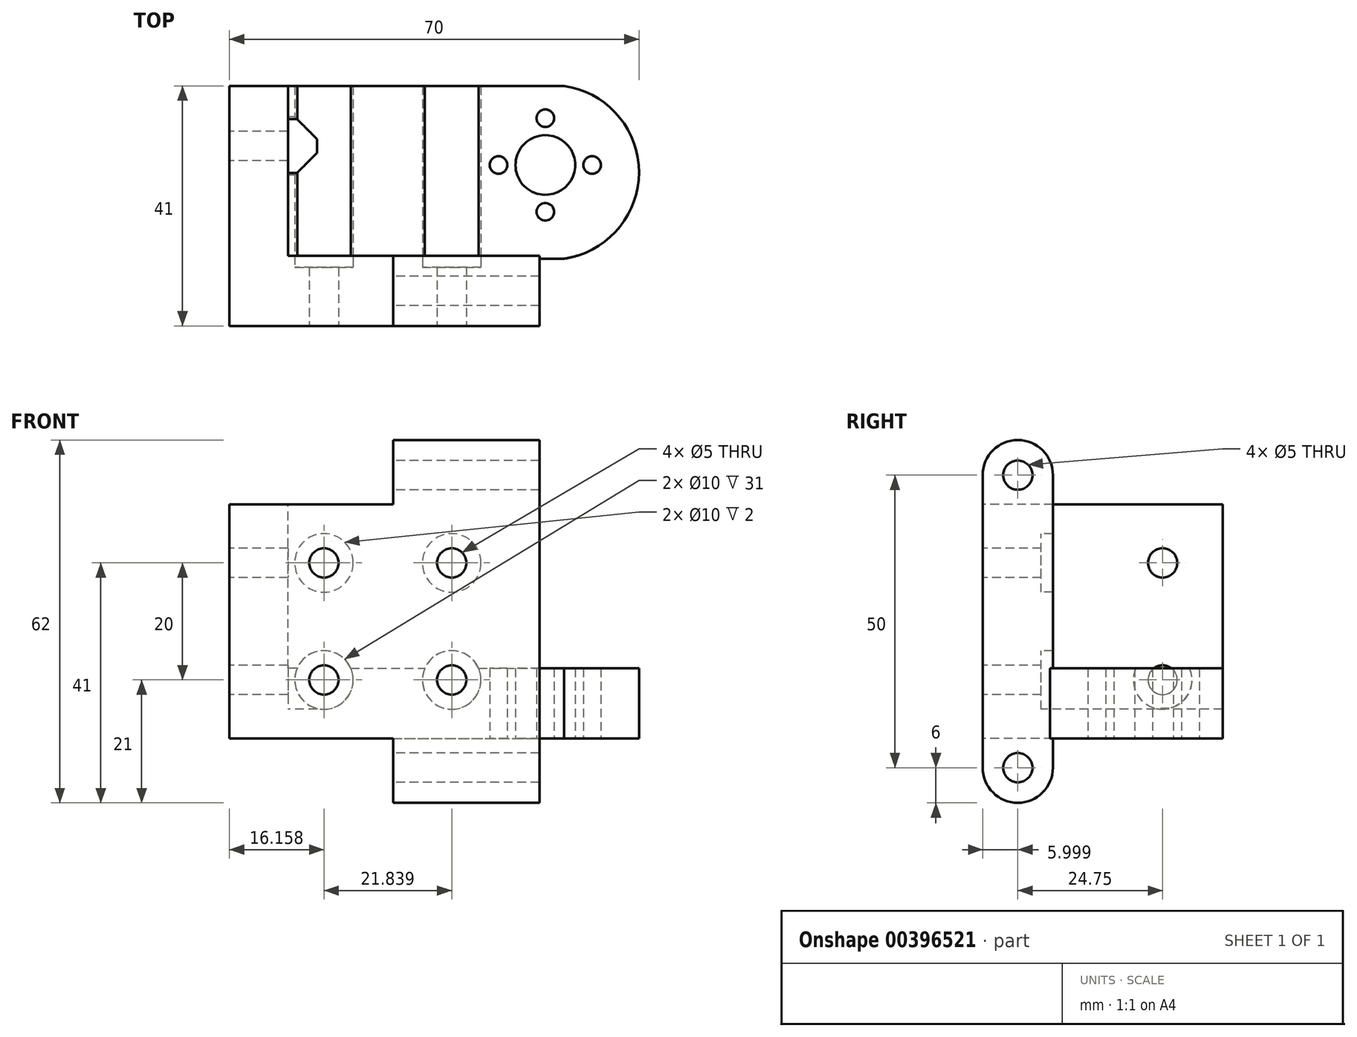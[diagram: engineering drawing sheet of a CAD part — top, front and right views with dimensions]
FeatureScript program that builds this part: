
annotation { "Feature Type Name" : "Feature", "Feature Type Description" : "" }
export const myFeature = defineFeature(function(context is Context, id is Id, definition is map)
    precondition{}
    {
        {
            var Q0;
            Q0=qCreatedBy(makeId("Top.planeOp"),FACE);
            var sketch = newSketch(context, id + "F0", { "sketchPlane" : qUnion([Q0])});
            skLineSegment(sketch, "E0.bottom", {"start": v(-287.66, 67.89) * mm, "end": v(-234.66, 67.89) * mm});
            skLineSegment(sketch, "E0.top", {"start": v(-287.66, 26.89) * mm, "end": v(-274.66, 26.89) * mm});
            skLineSegment(sketch, "E0.left", {"start": v(-287.66, 67.89) * mm, "end": v(-287.66, 26.89) * mm});
            skLineSegment(sketch, "E1.top", {"start": v(-234.66, 6.89) * mm, "end": v(-274.66, 6.89) * mm});
            skLineSegment(sketch, "E1.left", {"start": v(-234.66, 26.89) * mm, "end": v(-234.66, 6.89) * mm});
            skLineSegment(sketch, "E1.right", {"start": v(-274.66, 26.89) * mm, "end": v(-274.66, 6.89) * mm});
            skLineSegment(sketch, "E2.bottom", {"start": v(-234.66, 67.89) * mm, "end": v(-230.46, 67.89) * mm});
            skLineSegment(sketch, "E2.top", {"start": v(-234.66, 38.39) * mm, "end": v(-230.46, 38.39) * mm});
            skArc(sketch, "E3", {"start": v(-230.46, 38.39) * mm, "mid": v(-217.66, 53.14) * mm, "end": v(-230.46, 67.89) * mm});
            skLineSegment(sketch, "E4", {"start": v(-233.66, 54.39) * mm, "end": v(-287.66, 54.39) * mm, "construction": true});
            skCircle(sketch, "E5", {"center": v(-233.66, 54.39) * mm, "radius": 5.1 * mm});
            skLineSegment(sketch, "E6.trimOffspring", {"start": v(-234.66, 38.39) * mm, "end": v(-234.66, 26.89) * mm});
            skLineSegment(sketch, "E7", {"start": v(-233.66, 54.39) * mm, "end": v(-233.66, 62.39) * mm, "construction": true});
            skLineSegment(sketch, "E8", {"start": v(-233.66, 54.39) * mm, "end": v(-233.66, 46.39) * mm, "construction": true});
            skLineSegment(sketch, "E9", {"start": v(-233.66, 54.39) * mm, "end": v(-225.66, 54.39) * mm, "construction": true});
            skLineSegment(sketch, "E10", {"start": v(-233.66, 54.39) * mm, "end": v(-241.66, 54.39) * mm, "construction": true});
            skCircle(sketch, "E11", {"center": v(-241.66, 54.39) * mm, "radius": 1.5 * mm});
            skCircle(sketch, "E12", {"center": v(-233.66, 62.39) * mm, "radius": 1.5 * mm});
            skCircle(sketch, "E13", {"center": v(-225.66, 54.39) * mm, "radius": 1.5 * mm});
            skCircle(sketch, "E14", {"center": v(-233.66, 46.39) * mm, "radius": 1.5 * mm});
            skLineSegment(sketch, "E15", {"start": v(-233.66, 54.39) * mm, "end": v(-233.66, 26.89) * mm, "construction": true});
            skSolve(sketch);
        }
        {
            var Q0;
            Q0 = qSketchRegion(id + "F0", true);
            extrude(context, id + "F1", {"entities" : qUnion([Q0]), "depth" : 40 * mm});
        }
        {
            var Q0;
            Q0=makeQuery(id+"F1.opExtrude","CAP_FACE",FACE,{"disambiguationData":[OSD([sQuery(id+"F0.wireOp",EDGE,"E0.bottom"),sQuery(id+"F0.wireOp",EDGE,"E0.top"),sQuery(id+"F0.wireOp",EDGE,"E0.left"),sQuery(id+"F0.wireOp",EDGE,"E1.top"),sQuery(id+"F0.wireOp",EDGE,"E1.left"),sQuery(id+"F0.wireOp",EDGE,"E1.right"),sQuery(id+"F0.wireOp",EDGE,"E2.bottom"),sQuery(id+"F0.wireOp",EDGE,"E2.top"),sQuery(id+"F0.wireOp",EDGE,"E3"),sQuery(id+"F0.wireOp",EDGE,"E5"),sQuery(id+"F0.wireOp",EDGE,"E6.trimOffspring"),sQuery(id+"F0.wireOp",EDGE,"E11"),sQuery(id+"F0.wireOp",EDGE,"E12"),sQuery(id+"F0.wireOp",EDGE,"E13"),sQuery(id+"F0.wireOp",EDGE,"E14")])],"isStart":false});
            var sketch = newSketch(context, id + "F2", { "sketchPlane" : qUnion([Q0])});
            skCircle(sketch, "E16", {"center": v(-233.66, 54.39) * mm, "radius": 11.5 * mm});
            skSolve(sketch);
        }
        {
            var Q0;
            Q0 = qSketchRegion(id + "F2", true);
            extrude(context, id + "F3", {"entities" : qUnion([Q0]), "operationType" : NewBodyOperationType.REMOVE, "oppositeDirection" : true, "depth" : (40 - 12) * mm});
        }
        {
            var Q0;
            Q0=makeQuery(id+"F1.opExtrude","SWEPT_FACE",FACE,{"disambiguationData":[OSD([sQuery(id+"F0.wireOp",EDGE,"E0.left")])]});
            var sketch = newSketch(context, id + "F4", { "sketchPlane" : qUnion([Q0])});
            skLineSegment(sketch, "E17.bottom", {"start": v(-26.89, 20) * mm, "end": v(-38.89, 20) * mm, "construction": true});
            skLineSegment(sketch, "E17.top", {"start": v(-26.89, 45) * mm, "end": v(-38.89, 45) * mm, "construction": true});
            skLineSegment(sketch, "E17.left", {"start": v(-26.89, 20) * mm, "end": v(-26.89, 45) * mm});
            skLineSegment(sketch, "E17.right", {"start": v(-38.89, 20) * mm, "end": v(-38.89, 45) * mm});
            skLineSegment(sketch, "E18.MirrorCS", {"start": v(-38.89, 20) * mm, "end": v(-38.89, -5) * mm});
            skLineSegment(sketch, "E19.MirrorCS", {"start": v(-26.89, 20) * mm, "end": v(-26.89, -5) * mm});
            skLineSegment(sketch, "E20.MirrorCS", {"start": v(-26.89, -5) * mm, "end": v(-38.89, -5) * mm, "construction": true});
            skCircle(sketch, "E21", {"center": v(-32.89, 45) * mm, "radius": 6 * mm});
            skCircle(sketch, "E22", {"center": v(-32.89, -5) * mm, "radius": 6 * mm});
            skLineSegment(sketch, "E23", {"start": v(-32.89, 20) * mm, "end": v(-32.89, 51) * mm, "construction": true});
            skCircle(sketch, "E24", {"center": v(-32.89, 45) * mm, "radius": 2.5 * mm});
            skCircle(sketch, "E25", {"center": v(-32.89, -5) * mm, "radius": 2.5 * mm});
            skSolve(sketch);
        }
        {
            var Q0;
            Q0 = qSketchRegion(id + "F4", true);
            extrude(context, id + "F5", {"entities" : qUnion([Q0]), "operationType" : NewBodyOperationType.ADD, "oppositeDirection" : true, "depth" : 53 * mm, "hasSecondDirection" : true, "secondDirectionOppositeDirection" : true, "secondDirectionDepth" : (53 - 25) * mm});
        }
        {
            var Q0;
            Q0=makeQuery(id+"F1.opExtrude","SWEPT_FACE",FACE,{"disambiguationData":[OSD([sQuery(id+"F0.wireOp",EDGE,"E0.bottom"),sQuery(id+"F0.wireOp",EDGE,"E2.bottom")])]});
            var sketch = newSketch(context, id + "F6", { "sketchPlane" : qUnion([Q0])});
            skLineSegment(sketch, "E26.bottom", {"start": v(287.66, 40) * mm, "end": v(277.66, 40) * mm, "construction": true});
            skLineSegment(sketch, "E26.top", {"start": v(287.66, 0) * mm, "end": v(277.66, 0) * mm, "construction": true});
            skLineSegment(sketch, "E26.left", {"start": v(287.66, 40) * mm, "end": v(287.66, 0) * mm, "construction": true});
            skLineSegment(sketch, "E26.right", {"start": v(277.66, 40) * mm, "end": v(277.66, 0) * mm, "construction": true});
            skLineSegment(sketch, "E27.top", {"start": v(287.66, 12) * mm, "end": v(277.66, 12) * mm, "construction": true});
            skLineSegment(sketch, "E27.left", {"start": v(287.66, 0) * mm, "end": v(287.66, 12) * mm, "construction": true});
            skLineSegment(sketch, "E27.right", {"start": v(277.66, 0) * mm, "end": v(277.66, 12) * mm, "construction": true});
            skLineSegment(sketch, "E28.bottom", {"start": v(277.66, 12) * mm, "end": v(200.17, 12) * mm});
            skLineSegment(sketch, "E28.top", {"start": v(277.66, 42.16) * mm, "end": v(200.17, 42.16) * mm});
            skLineSegment(sketch, "E28.left", {"start": v(277.66, 12) * mm, "end": v(277.66, 42.16) * mm});
            skLineSegment(sketch, "E28.right", {"start": v(200.17, 12) * mm, "end": v(200.17, 42.16) * mm});
            skSolve(sketch);
        }
        {
            var Q0;
            Q0 = qSketchRegion(id + "F6", true);
            extrude(context, id + "F7", {"entities" : qUnion([Q0]), "operationType" : NewBodyOperationType.REMOVE, "oppositeDirection" : true, "depth" : 29 * mm});
        }
        {
            var Q0;
            Q0=makeQuery(id+"F1.opExtrude","SWEPT_FACE",FACE,{"disambiguationData":[OSD([sQuery(id+"F0.wireOp",EDGE,"E2.top")])]});
            var sketch = newSketch(context, id + "F8", { "sketchPlane" : qUnion([Q0])});
            skLineSegment(sketch, "E29.bottom", {"start": v(-234.66, 40) * mm, "end": v(-228, 40) * mm});
            skLineSegment(sketch, "E29.top", {"start": v(-234.66, 12) * mm, "end": v(-228, 12) * mm});
            skLineSegment(sketch, "E29.left", {"start": v(-234.66, 40) * mm, "end": v(-234.66, 12) * mm});
            skLineSegment(sketch, "E29.right", {"start": v(-228, 40) * mm, "end": v(-228, 12) * mm});
            skSolve(sketch);
        }
        {
            var Q0;
            Q0 = qSketchRegion(id + "F8", true);
            extrude(context, id + "F9", {"entities" : qUnion([Q0]), "operationType" : NewBodyOperationType.REMOVE, "oppositeDirection" : true, "depth" : 25 * mm});
        }
        {
            var Q0;
            Q0=makeQuery(id+"F1.opExtrude","SWEPT_FACE",FACE,{"disambiguationData":[OSD([sQuery(id+"F0.wireOp",EDGE,"E1.right")])]});
            var sketch = newSketch(context, id + "F10", { "sketchPlane" : qUnion([Q0])});
            skLineSegment(sketch, "E30.bottom", {"start": v(-26.89, 0) * mm, "end": v(-1.07, 0) * mm});
            skLineSegment(sketch, "E30.top", {"start": v(-26.89, 54.04) * mm, "end": v(-1.07, 54.04) * mm});
            skLineSegment(sketch, "E30.left", {"start": v(-26.89, 0) * mm, "end": v(-26.89, 54.04) * mm});
            skLineSegment(sketch, "E30.right", {"start": v(-1.07, 0) * mm, "end": v(-1.07, 54.04) * mm});
            skSolve(sketch);
        }
        {
            var Q0;
            Q0 = qSketchRegion(id + "F10", true);
            extrude(context, id + "F11", {"entities" : qUnion([Q0]), "operationType" : NewBodyOperationType.REMOVE, "oppositeDirection" : true, "depth" : 50 * mm});
        }
        {
            var Q0;
            {var subQ2=sQuery(id+"F4.wireOp",EDGE,"E22");var subQ3=sQuery(id+"F4.wireOp",EDGE,"E21");var subQ4=sQuery(id+"F4.wireOp",EDGE,"E19.MirrorCS");var subQ7=sQuery(id+"F4.wireOp",EDGE,"E17.left");var subQ24=sQuery(id+"F0.wireOp",EDGE,"E0.top");var subQ26=makeQuery(id+"F5.opExtrude","SWEPT_FACE",FACE,{"disambiguationData":[OSD([subQ7,subQ4])]});Q0=makeQuery(id+"F11.boolean.opBoolean","MERGE",FACE,{"derivedFrom":[makeQuery(id+"F1.opExtrude","SWEPT_FACE",FACE,{"disambiguationData":[OSD([subQ24])]}),makeQuery(id+"F5.boolean.opBoolean","SPLIT",FACE,{"disambiguationData":[TD([makeQuery(id+"F5.opExtrude","SWEPT_FACE",FACE,{"disambiguationData":[OSD([subQ3])]})])],"derivedFrom":subQ26}),makeQuery(id+"F5.boolean.opBoolean","SPLIT",FACE,{"disambiguationData":[TD([makeQuery(id+"F5.opExtrude","SWEPT_FACE",FACE,{"disambiguationData":[OSD([subQ2])]})])],"derivedFrom":subQ26}),makeQuery(id+"F11.opExtrude","SWEPT_FACE",FACE,{"disambiguationData":[OSD([sQuery(id+"F10.wireOp",EDGE,"E30.left")])]})]});}
            var sketch = newSketch(context, id + "F12", { "sketchPlane" : qUnion([Q0])});
            skLineSegment(sketch, "E31.bottom", {"start": v(-287.66, 40) * mm, "end": v(-234.66, 40) * mm, "construction": true});
            skLineSegment(sketch, "E31.top", {"start": v(-287.66, 0) * mm, "end": v(-234.66, 0) * mm, "construction": true});
            skLineSegment(sketch, "E31.left", {"start": v(-287.66, 40) * mm, "end": v(-287.66, 0) * mm, "construction": true});
            skLineSegment(sketch, "E31.right", {"start": v(-234.66, 40) * mm, "end": v(-234.66, 0) * mm, "construction": true});
            skLineSegment(sketch, "E32", {"start": v(-287.66, 20) * mm, "end": v(-234.66, 20) * mm, "construction": true});
            skLineSegment(sketch, "E33", {"start": v(-261.16, 40) * mm, "end": v(-261.16, 20) * mm, "construction": true});
            skLineSegment(sketch, "E34", {"start": v(-261.16, 20) * mm, "end": v(-261.16, 0) * mm, "construction": true});
            skLineSegment(sketch, "E35", {"start": v(-261.16, 30) * mm, "end": v(-287.66, 30) * mm, "construction": true});
            skLineSegment(sketch, "E36", {"start": v(-261.16, 10) * mm, "end": v(-287.66, 10) * mm, "construction": true});
            skLineSegment(sketch, "E37", {"start": v(-261.16, 30) * mm, "end": v(-234.66, 30) * mm, "construction": true});
            skLineSegment(sketch, "E38", {"start": v(-261.16, 10) * mm, "end": v(-234.66, 10) * mm, "construction": true});
            skLineSegment(sketch, "E39", {"start": v(-234.66, 35.46) * mm, "end": v(-249.66, 35.46) * mm, "construction": true});
            skCircle(sketch, "E40", {"center": v(-249.66, 30) * mm, "radius": 2.5 * mm});
            skCircle(sketch, "E41", {"center": v(-249.66, 10) * mm, "radius": 2.5 * mm});
            skCircle(sketch, "E42", {"center": v(-271.5, 30) * mm, "radius": 2.5 * mm});
            skCircle(sketch, "E43", {"center": v(-271.5, 10) * mm, "radius": 2.5 * mm});
            skSolve(sketch);
        }
        {
            var Q0;
            Q0 = qSketchRegion(id + "F12", true);
            extrude(context, id + "F13", {"entities" : qUnion([Q0]), "operationType" : NewBodyOperationType.REMOVE, "oppositeDirection" : true, "depth" : 50 * mm});
        }
        {
            var Q0;
            Q0=makeQuery(id+"F1.opExtrude","SWEPT_FACE",FACE,{"disambiguationData":[OSD([sQuery(id+"F0.wireOp",EDGE,"E0.left")])]});
            var sketch = newSketch(context, id + "F14", { "sketchPlane" : qUnion([Q0])});
            skLineSegment(sketch, "E44.bottom", {"start": v(-67.89, 40) * mm, "end": v(-26.89, 40) * mm, "construction": true});
            skLineSegment(sketch, "E44.top", {"start": v(-67.89, 0) * mm, "end": v(-26.89, 0) * mm, "construction": true});
            skLineSegment(sketch, "E44.left", {"start": v(-67.89, 40) * mm, "end": v(-67.89, 0) * mm, "construction": true});
            skLineSegment(sketch, "E44.right", {"start": v(-26.89, 40) * mm, "end": v(-26.89, 0) * mm, "construction": true});
            skLineSegment(sketch, "E45", {"start": v(-67.89, 20) * mm, "end": v(-26.89, 20) * mm, "construction": true});
            skLineSegment(sketch, "E46", {"start": v(-47.39, 40) * mm, "end": v(-47.39, 20) * mm, "construction": true});
            skLineSegment(sketch, "E47", {"start": v(-47.39, 20) * mm, "end": v(-47.39, 0) * mm, "construction": true});
            skLineSegment(sketch, "E48", {"start": v(-47.39, 30) * mm, "end": v(-67.89, 30) * mm, "construction": true});
            skLineSegment(sketch, "E49", {"start": v(-47.39, 10) * mm, "end": v(-67.89, 10) * mm, "construction": true});
            skCircle(sketch, "E50", {"center": v(-57.64, 30) * mm, "radius": 2.5 * mm});
            skCircle(sketch, "E51", {"center": v(-57.64, 10) * mm, "radius": 2.5 * mm});
            skSolve(sketch);
        }
        {
            var Q0;
            Q0 = qSketchRegion(id + "F14", true);
            extrude(context, id + "F15", {"entities" : qUnion([Q0]), "operationType" : NewBodyOperationType.REMOVE, "oppositeDirection" : true, "depth" : 15 * mm});
        }
        {
            var Q0;
            {var subQ2=sQuery(id+"F4.wireOp",EDGE,"E22");var subQ3=sQuery(id+"F4.wireOp",EDGE,"E21");var subQ4=sQuery(id+"F4.wireOp",EDGE,"E19.MirrorCS");var subQ7=sQuery(id+"F4.wireOp",EDGE,"E17.left");var subQ24=sQuery(id+"F0.wireOp",EDGE,"E0.top");var subQ26=makeQuery(id+"F5.opExtrude","SWEPT_FACE",FACE,{"disambiguationData":[OSD([subQ7,subQ4])]});Q0=makeQuery(id+"F11.boolean.opBoolean","MERGE",FACE,{"derivedFrom":[makeQuery(id+"F1.opExtrude","SWEPT_FACE",FACE,{"disambiguationData":[OSD([subQ24])]}),makeQuery(id+"F5.boolean.opBoolean","SPLIT",FACE,{"disambiguationData":[TD([makeQuery(id+"F5.opExtrude","SWEPT_FACE",FACE,{"disambiguationData":[OSD([subQ3])]})])],"derivedFrom":subQ26}),makeQuery(id+"F5.boolean.opBoolean","SPLIT",FACE,{"disambiguationData":[TD([makeQuery(id+"F5.opExtrude","SWEPT_FACE",FACE,{"disambiguationData":[OSD([subQ2])]})])],"derivedFrom":subQ26}),makeQuery(id+"F11.opExtrude","SWEPT_FACE",FACE,{"disambiguationData":[OSD([sQuery(id+"F10.wireOp",EDGE,"E30.left")])]})]});}
            var sketch = newSketch(context, id + "F16", { "sketchPlane" : qUnion([Q0])});
            skCircle(sketch, "E52", {"center": v(-271.5, 10) * mm, "radius": 5 * mm});
            skCircle(sketch, "E53", {"center": v(-249.66, 10) * mm, "radius": 5 * mm});
            skCircle(sketch, "E54", {"center": v(-271.5, 30) * mm, "radius": 5 * mm});
            skCircle(sketch, "E55", {"center": v(-249.66, 30) * mm, "radius": 5 * mm});
            skSolve(sketch);
        }
        {
            var Q0;
            Q0 = qSketchRegion(id + "F16", true);
            extrude(context, id + "F17", {"entities" : qUnion([Q0]), "operationType" : NewBodyOperationType.REMOVE, "oppositeDirection" : true, "depth" : 50 * mm, "hasSecondDirection" : true, "secondDirectionOppositeDirection" : true, "secondDirectionDepth" : 10 * mm});
        }
        {
            var Q0;
            Q0=makeQuery(id+"F1.opExtrude","SWEPT_FACE",FACE,{"disambiguationData":[OSD([sQuery(id+"F0.wireOp",EDGE,"E0.left")])]});
            var sketch = newSketch(context, id + "F18", { "sketchPlane" : qUnion([Q0])});
            skCircle(sketch, "E56", {"center": v(-57.64, 10) * mm, "radius": 5 * mm});
            skSolve(sketch);
        }
        {
            var Q0;
            Q0 = qSketchRegion(id + "F18", true);
            extrude(context, id + "F19", {"entities" : qUnion([Q0]), "operationType" : NewBodyOperationType.REMOVE, "oppositeDirection" : true, "depth" : 15 * mm, "hasSecondDirection" : true, "secondDirectionOppositeDirection" : true, "secondDirectionDepth" : 10 * mm});
        }
    });
